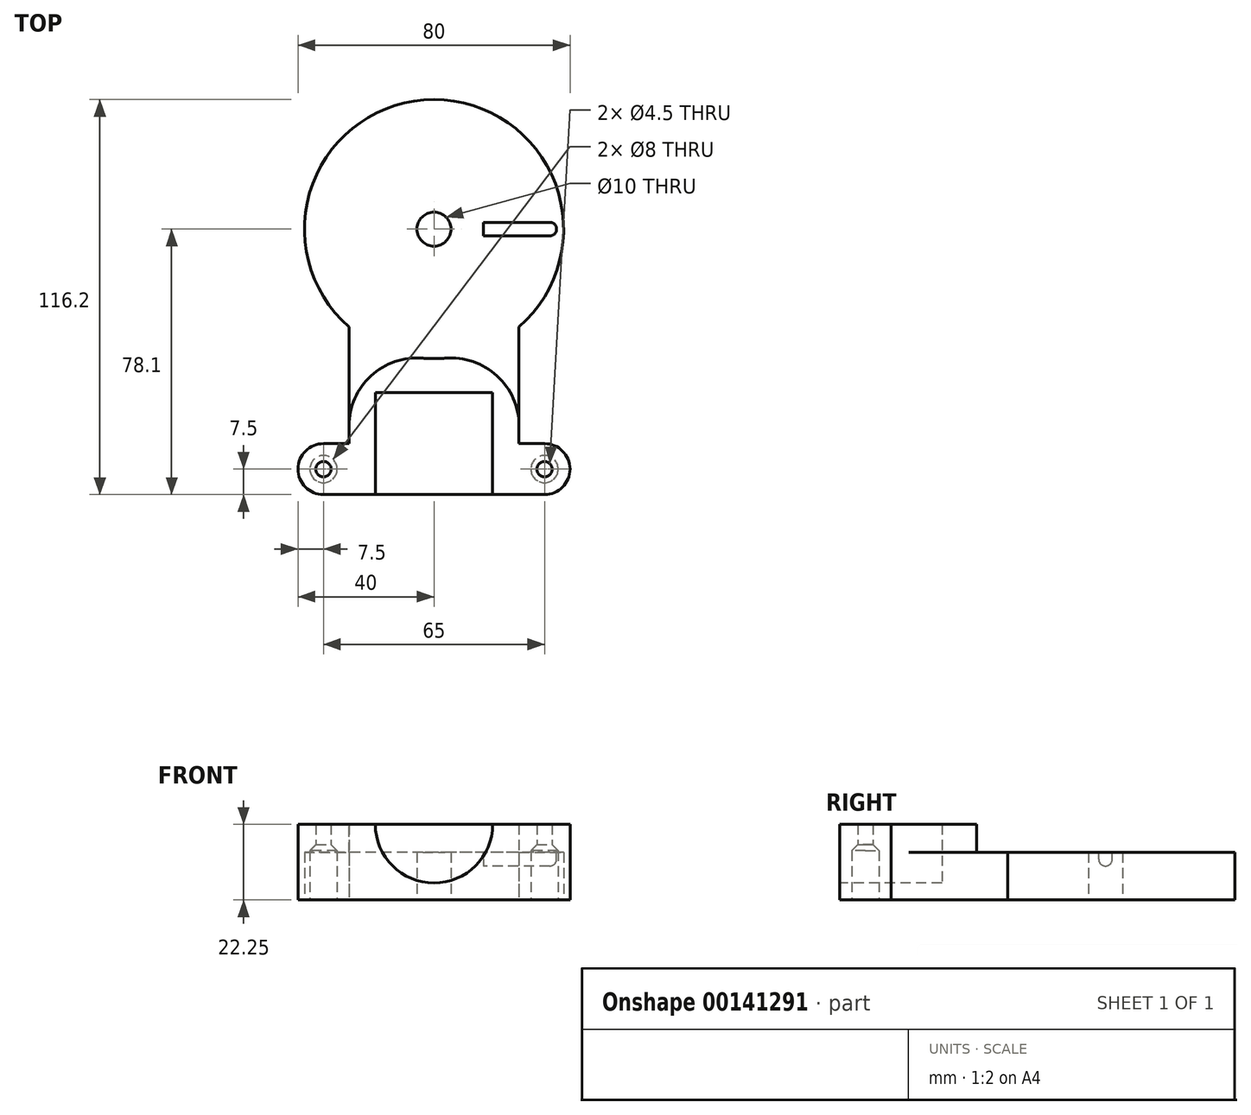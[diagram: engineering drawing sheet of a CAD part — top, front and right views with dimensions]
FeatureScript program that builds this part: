
annotation { "Feature Type Name" : "Feature", "Feature Type Description" : "" }
export const myFeature = defineFeature(function(context is Context, id is Id, definition is map)
    precondition{}
    {
        {
            var Q0;
            Q0=qCreatedBy(makeId("Top.planeOp"),FACE);
            var sketch = newSketch(context, id + "F0", { "sketchPlane" : qUnion([Q0])});
            skArc(sketch, "E0", {"start": v(38.1, 0) * mm, "mid": v(0, 38.1) * mm, "end": v(-38.1, 0) * mm});
            skCircle(sketch, "E1", {"center": v(0, 0) * mm, "radius": 5 * mm});
            skArc(sketch, "E2", {"start": v(-38.1, 0) * mm, "mid": v(0, -38.1) * mm, "end": v(38.1, 0) * mm});
            skSolve(sketch);
        }
        {
            var Q0;
            Q0 = qSketchRegion(id + "F0", true);
            extrude(context, id + "F1", {"entities" : qUnion([Q0]), "depth" : 14 * mm});
        }
        {
            var Q0;
            Q0=makeQuery(id+"F1.opExtrude","CAP_FACE",FACE,{"disambiguationData":[OSD([sQuery(id+"F0.wireOp",EDGE,"E0"),sQuery(id+"F0.wireOp",EDGE,"E1"),sQuery(id+"F0.wireOp",EDGE,"E2")])],"isStart":false});
            var sketch = newSketch(context, id + "F2", { "sketchPlane" : qUnion([Q0])});
            skLineSegment(sketch, "E3.bottom", {"start": v(34.03, -2) * mm, "end": v(14.53, -2) * mm});
            skLineSegment(sketch, "E3.top", {"start": v(34.03, 2) * mm, "end": v(14.53, 2) * mm});
            skLineSegment(sketch, "E3.left", {"start": v(36.02, -2) * mm, "end": v(36.02, 2) * mm, "construction": true});
            skLineSegment(sketch, "E3.right", {"start": v(14.53, -2) * mm, "end": v(14.53, 2) * mm});
            skPoint(sketch, "E3.middle", {"position": v(25.28, 0) * mm});
            skArc(sketch, "E4", {"start": v(34.03, 2) * mm, "mid": v(36.03, 0) * mm, "end": v(34.03, -2) * mm});
            skSolve(sketch);
        }
        {
            var Q0;
            Q0 = qSketchRegion(id + "F2", true);
            extrude(context, id + "F3", {"entities" : qUnion([Q0]), "operationType" : NewBodyOperationType.REMOVE, "oppositeDirection" : true, "depth" : 4 * mm});
        }
        {
            var Q0;
            Q0=makeQuery(id+"F3.boolean.opBoolean","COPY",EDGE,{"derivedFrom":makeQuery(id+"F3.opExtrude","CAP_EDGE",EDGE,{"disambiguationData":[OSD([sQuery(id+"F2.wireOp",EDGE,"E3.top")])],"isStart":false})});
            fillet(context, id + "F4", {"entities" : qUnion([Q0]), "radius" : 2 * mm, "tangentPropagation" : true, "allowEdgeOverflow" : false});
        }
        {
            var Q0;
            Q0=qCreatedBy(makeId("Top.planeOp"),FACE);
            var sketch = newSketch(context, id + "F5", { "sketchPlane" : qUnion([Q0])});
            skArc(sketch, "E5", {"start": v(-25, -28.75) * mm, "mid": v(-13.35, -35.69) * mm, "end": v(0, -38.1) * mm});
            skLineSegment(sketch, "E6", {"start": v(-25, -28.75) * mm, "end": v(-25, -63.1) * mm});
            skLineSegment(sketch, "E7", {"start": v(-25, -78.1) * mm, "end": v(0, -78.1) * mm});
            skArc(sketch, "E8.MirrorCS", {"start": v(25, -28.75) * mm, "mid": v(13.35, -35.69) * mm, "end": v(0, -38.1) * mm});
            skLineSegment(sketch, "E9.MirrorCS", {"start": v(25, -28.75) * mm, "end": v(25, -63.1) * mm});
            skLineSegment(sketch, "E10.MirrorCS", {"start": v(25, -78.1) * mm, "end": v(0, -78.1) * mm});
            skLineSegment(sketch, "E11", {"start": v(-25, -63.1) * mm, "end": v(-40, -63.1) * mm});
            skLineSegment(sketch, "E12", {"start": v(-40, -63.1) * mm, "end": v(-40, -78.1) * mm});
            skLineSegment(sketch, "E13", {"start": v(-40, -78.1) * mm, "end": v(-25, -78.1) * mm});
            skLineSegment(sketch, "E14.MirrorCS", {"start": v(25, -63.1) * mm, "end": v(40, -63.1) * mm});
            skLineSegment(sketch, "E15.MirrorCS", {"start": v(40, -63.1) * mm, "end": v(40, -78.1) * mm});
            skLineSegment(sketch, "E16.MirrorCS", {"start": v(40, -78.1) * mm, "end": v(25, -78.1) * mm});
            skPoint(sketch, "E17.orphan", {"position": v(25, -78.1) * mm});
            skCircle(sketch, "E18", {"center": v(-32.5, -70.6) * mm, "radius": 2.25 * mm});
            skCircle(sketch, "E19.MirrorC", {"center": v(32.5, -70.6) * mm, "radius": 2.25 * mm});
            skSolve(sketch);
        }
        {
            var Q0;
            Q0 = qSketchRegion(id + "F5", true);
            extrude(context, id + "F6", {"entities" : qUnion([Q0]), "operationType" : NewBodyOperationType.ADD, "depth" : 22.25 * mm});
        }
        {
            var Q0;
            Q0=makeQuery(id+"F6.opExtrude","SWEPT_FACE",FACE,{"disambiguationData":[OSD([sQuery(id+"F5.wireOp",EDGE,"E7"),sQuery(id+"F5.wireOp",EDGE,"E10.MirrorCS")])]});
            var sketch = newSketch(context, id + "F7", { "sketchPlane" : qUnion([Q0])});
            skCircle(sketch, "E20", {"center": v(0, 22.25) * mm, "radius": 17.25 * mm});
            skSolve(sketch);
        }
        {
            var Q0;
            Q0 = qSketchRegion(id + "F7", true);
            extrude(context, id + "F8", {"entities" : qUnion([Q0]), "operationType" : NewBodyOperationType.REMOVE, "oppositeDirection" : true, "depth" : 30 * mm});
        }
        {
            var Q0;
            Q0=qCreatedBy(makeId("Top.planeOp"),FACE);
            var sketch = newSketch(context, id + "F9", { "sketchPlane" : qUnion([Q0])});
            skCircle(sketch, "E21", {"center": v(-32.5, -70.6) * mm, "radius": 4 * mm});
            skCircle(sketch, "E22.MirrorC", {"center": v(32.5, -70.6) * mm, "radius": 4 * mm});
            skSolve(sketch);
        }
        {
            var Q0;
            Q0 = qSketchRegion(id + "F9", true);
            extrude(context, id + "F10", {"entities" : qUnion([Q0]), "operationType" : NewBodyOperationType.REMOVE, "depth" : 17 * mm});
        }
        {
            var Q0;
            Q0=makeQuery(id+"F10.boolean.opBoolean","COPY",EDGE,{"derivedFrom":makeQuery(id+"F10.opExtrude","CAP_EDGE",EDGE,{"disambiguationData":[OSD([sQuery(id+"F9.wireOp",EDGE,"E21")])],"isStart":false})});
            var Q1;
            Q1=makeQuery(id+"F10.boolean.opBoolean","COPY",EDGE,{"derivedFrom":makeQuery(id+"F10.opExtrude","CAP_EDGE",EDGE,{"disambiguationData":[OSD([sQuery(id+"F9.wireOp",EDGE,"E22.MirrorC")])],"isStart":false})});
            chamfer(context, id + "F11", {"entities" : qUnion([Q0, Q1]), "width" : 2.5 * mm, "tangentPropagation" : true});
        }
        {
            var Q0;
            {var subQ0=sQuery(id+"F5.wireOp",EDGE,"E5");var subQ1=sQuery(id+"F5.wireOp",EDGE,"E6");Q0=makeQuery(id+"F6.boolean.opBoolean","SPLIT",EDGE,{"disambiguationData":[topologyDisambiguationEdgeConnected([makeQuery(id+"F6.opExtrude","SWEPT_FACE",FACE,{"disambiguationData":[OSD([subQ0,sQuery(id+"F5.wireOp",EDGE,"E8.MirrorCS")])]})])],"derivedFrom":makeQuery(id+"F6.opExtrude","SWEPT_EDGE",EDGE,{"disambiguationData":[OSD([subQ0,subQ1])]})});}
            var Q1;
            {var subQ0=sQuery(id+"F5.wireOp",EDGE,"E8.MirrorCS");var subQ1=sQuery(id+"F5.wireOp",EDGE,"E9.MirrorCS");Q1=makeQuery(id+"F6.boolean.opBoolean","SPLIT",EDGE,{"disambiguationData":[topologyDisambiguationEdgeConnected([makeQuery(id+"F6.opExtrude","SWEPT_FACE",FACE,{"disambiguationData":[OSD([sQuery(id+"F5.wireOp",EDGE,"E5"),subQ0])]})])],"derivedFrom":makeQuery(id+"F6.opExtrude","SWEPT_EDGE",EDGE,{"disambiguationData":[OSD([subQ0,subQ1])]})});}
            fillet(context, id + "F12", {"entities" : qUnion([Q0, Q1]), "radius" : 20 * mm, "tangentPropagation" : true, "allowEdgeOverflow" : false});
        }
        {
            var Q0;
            Q0=makeQuery(id+"F6.opExtrude","SWEPT_EDGE",EDGE,{"disambiguationData":[OSD([sQuery(id+"F5.wireOp",EDGE,"E11"),sQuery(id+"F5.wireOp",EDGE,"E12")])]});
            var Q1;
            Q1=makeQuery(id+"F6.opExtrude","SWEPT_EDGE",EDGE,{"disambiguationData":[OSD([sQuery(id+"F5.wireOp",EDGE,"E12"),sQuery(id+"F5.wireOp",EDGE,"E13")])]});
            var Q2;
            Q2=makeQuery(id+"F6.opExtrude","SWEPT_EDGE",EDGE,{"disambiguationData":[OSD([sQuery(id+"F5.wireOp",EDGE,"E15.MirrorCS"),sQuery(id+"F5.wireOp",EDGE,"E16.MirrorCS")])]});
            var Q3;
            Q3=makeQuery(id+"F6.opExtrude","SWEPT_EDGE",EDGE,{"disambiguationData":[OSD([sQuery(id+"F5.wireOp",EDGE,"E14.MirrorCS"),sQuery(id+"F5.wireOp",EDGE,"E15.MirrorCS")])]});
            fillet(context, id + "F13", {"entities" : qUnion([Q0, Q1, Q2, Q3]), "radius" : 7.5 * mm, "tangentPropagation" : true, "allowEdgeOverflow" : false});
        }
    });
